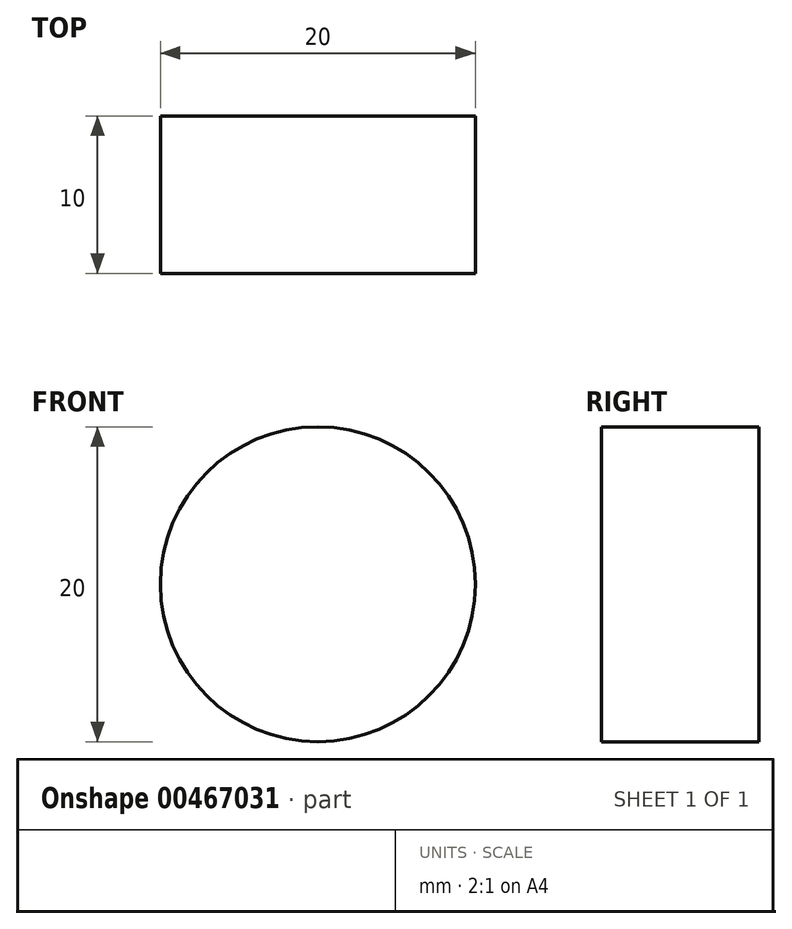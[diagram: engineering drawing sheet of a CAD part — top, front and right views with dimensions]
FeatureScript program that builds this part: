
annotation { "Feature Type Name" : "Feature", "Feature Type Description" : "" }
export const myFeature = defineFeature(function(context is Context, id is Id, definition is map)
    precondition{}
    {
        {
            var Q0;
            Q0=qCreatedBy(makeId("Front.planeOp"),FACE);
            var sketch = newSketch(context, id + "F0", { "sketchPlane" : qUnion([Q0])});
            skCircle(sketch, "E0", {"center": v(0, 0) * mm, "radius": 10 * mm});
            skSolve(sketch);
        }
        {
            var Q0;
            Q0 = qSketchRegion(id + "F0", true);
            extrude(context, id + "F1", {"entities" : qUnion([Q0]), "endBound" : BoundingType.SYMMETRIC, "oppositeDirection" : true, "depth" : 10 * mm});
        }
    });
